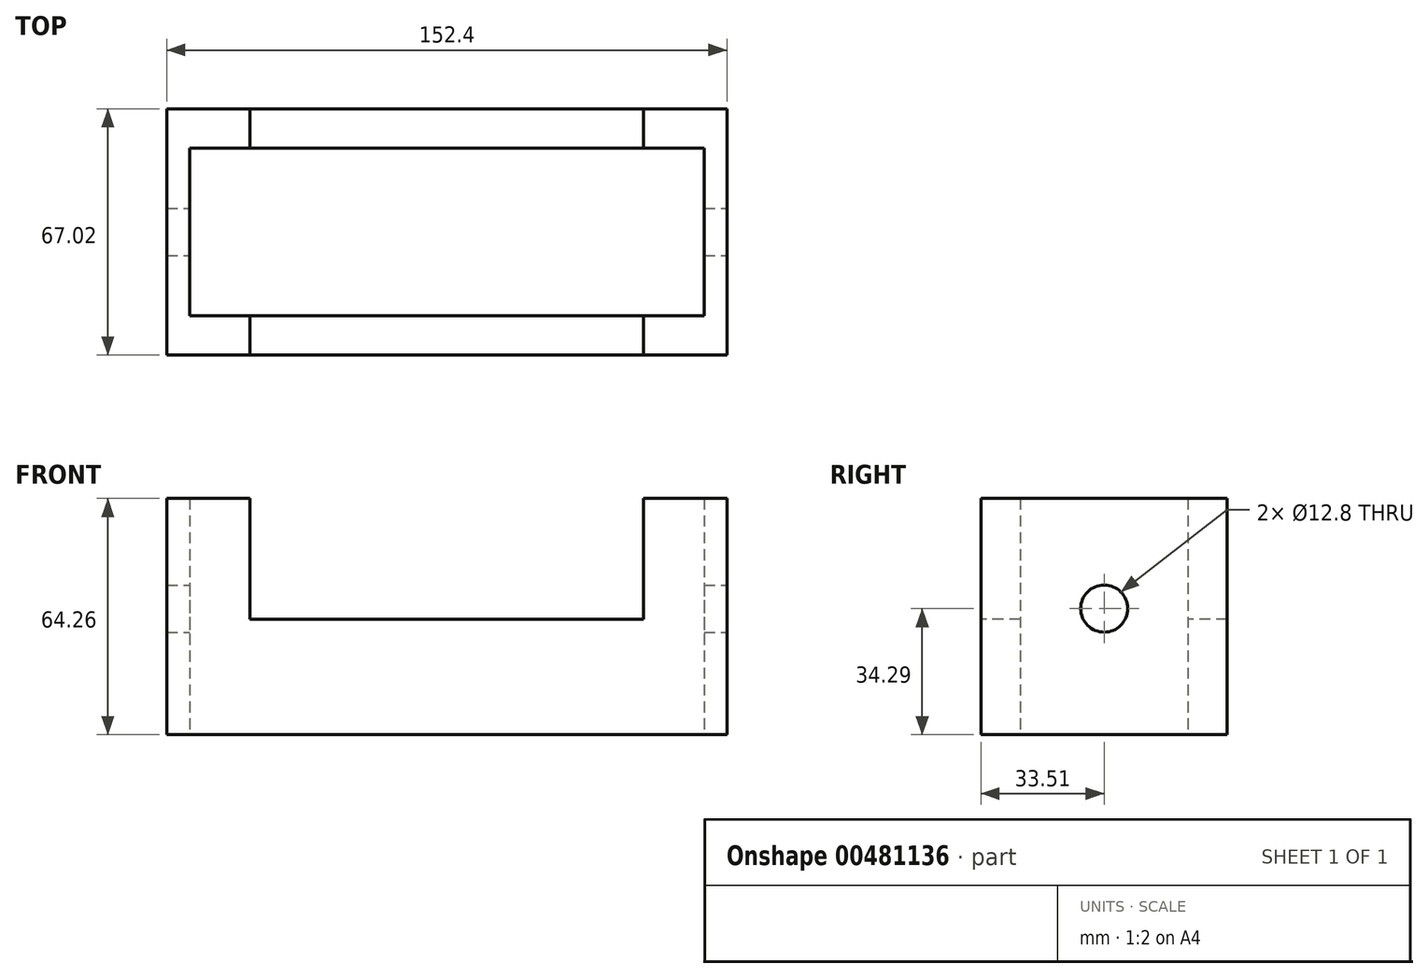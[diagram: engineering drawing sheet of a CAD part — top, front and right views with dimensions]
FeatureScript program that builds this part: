
annotation { "Feature Type Name" : "Feature", "Feature Type Description" : "" }
export const myFeature = defineFeature(function(context is Context, id is Id, definition is map)
    precondition{}
    {
        {
            var Q0;
            Q0=qCreatedBy(makeId("Top.planeOp"),FACE);
            var sketch = newSketch(context, id + "F0", { "sketchPlane" : qUnion([Q0])});
            skLineSegment(sketch, "E0.bottom", {"start": v(76.2, -33.5) * mm, "end": v(-76.2, -33.5) * mm});
            skLineSegment(sketch, "E0.top", {"start": v(76.2, 33.5) * mm, "end": v(-76.2, 33.5) * mm});
            skLineSegment(sketch, "E0.left", {"start": v(76.2, -33.5) * mm, "end": v(76.2, 33.5) * mm});
            skLineSegment(sketch, "E0.right", {"start": v(-76.2, -33.5) * mm, "end": v(-76.2, 33.5) * mm});
            skPoint(sketch, "E0.middle", {"position": v(0, 0) * mm});
            skLineSegment(sketch, "E1.bottom", {"start": v(69.98, -22.78) * mm, "end": v(-69.98, -22.78) * mm});
            skLineSegment(sketch, "E1.top", {"start": v(69.98, 22.78) * mm, "end": v(-69.98, 22.78) * mm});
            skLineSegment(sketch, "E1.left", {"start": v(69.98, -22.78) * mm, "end": v(69.98, 22.78) * mm});
            skLineSegment(sketch, "E1.right", {"start": v(-69.98, -22.78) * mm, "end": v(-69.98, 22.78) * mm});
            skSolve(sketch);
        }
        {
            var Q0;
            Q0=makeQuery(id+"F0.imprint","IMPRINT",FACE,{"disambiguationData":[TD([[makeQuery(id+"F0.imprint","IMPRINT",EDGE,{"derivedFrom":sQuery(id+"F0.wireOp",EDGE,"E0.bottom")}),-1.0]])]});
            extrude(context, id + "F1", {"entities" : qUnion([Q0]), "depth" : 64.26 * mm});
        }
        {
            var Q0;
            Q0=makeQuery(id+"F1.opExtrude","SWEPT_FACE",FACE,{"disambiguationData":[OSD([sQuery(id+"F0.wireOp",EDGE,"E0.bottom")])]});
            var sketch = newSketch(context, id + "F2", { "sketchPlane" : qUnion([Q0])});
            skLineSegment(sketch, "E2.bottom", {"start": v(-53.54, 64.26) * mm, "end": v(53.54, 64.26) * mm});
            skLineSegment(sketch, "E2.top", {"start": v(-53.54, 31.36) * mm, "end": v(53.54, 31.36) * mm});
            skLineSegment(sketch, "E2.left", {"start": v(-53.54, 64.26) * mm, "end": v(-53.54, 31.36) * mm});
            skLineSegment(sketch, "E2.right", {"start": v(53.54, 64.26) * mm, "end": v(53.54, 31.36) * mm});
            skSolve(sketch);
        }
        {
            var Q0;
            Q0 = qSketchRegion(id + "F2", true);
            extrude(context, id + "F3", {"entities" : qUnion([Q0]), "operationType" : NewBodyOperationType.REMOVE, "oppositeDirection" : true, "depth" : 90.17 * mm});
        }
        {
            var Q0;
            Q0=makeQuery(id+"F1.opExtrude","SWEPT_FACE",FACE,{"disambiguationData":[OSD([sQuery(id+"F0.wireOp",EDGE,"E0.left")])]});
            var sketch = newSketch(context, id + "F4", { "sketchPlane" : qUnion([Q0])});
            skCircle(sketch, "E3", {"center": v(0, 34.3) * mm, "radius": 6.4 * mm});
            skSolve(sketch);
        }
        {
            var Q0;
            Q0 = qSketchRegion(id + "F4", true);
            extrude(context, id + "F5", {"entities" : qUnion([Q0]), "operationType" : NewBodyOperationType.REMOVE, "oppositeDirection" : true, "depth" : 169.93 * mm});
        }
    });
